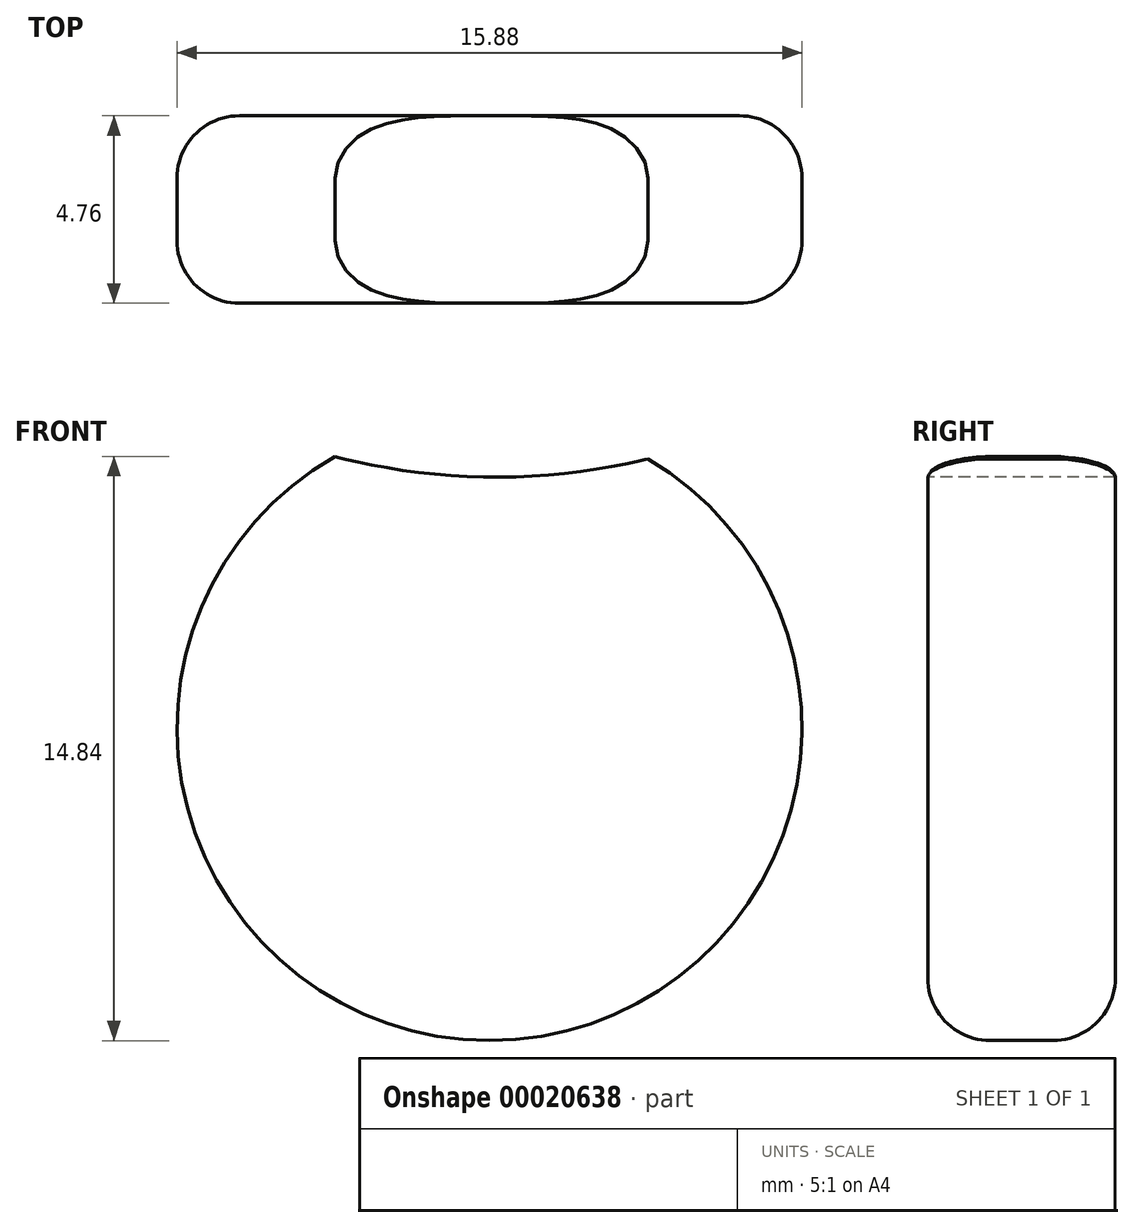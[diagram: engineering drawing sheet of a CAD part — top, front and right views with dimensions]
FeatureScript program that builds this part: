
annotation { "Feature Type Name" : "Feature", "Feature Type Description" : "" }
export const myFeature = defineFeature(function(context is Context, id is Id, definition is map)
    precondition{}
    {
        {
            var Q0;
            Q0=qCreatedBy(makeId("Front.planeOp"),FACE);
            var sketch = newSketch(context, id + "F0", { "sketchPlane" : qUnion([Q0])});
            skCircle(sketch, "E0", {"center": v(0, 0) * mm, "radius": 7.94 * mm});
            skSolve(sketch);
        }
        {
            var Q0;
            Q0=makeQuery(id+"F0.imprint","IMPRINT",FACE,{"disambiguationData":[TD([[makeQuery(id+"F0.imprint","IMPRINT",EDGE,{"derivedFrom":sQuery(id+"F0.wireOp",EDGE,"E0")}),1.0]])]});
            var sketch = newSketch(context, id + "F1", { "sketchPlane" : qUnion([Q0])});
            skSolve(sketch);
        }
        {
            var Q0;
            Q0 = qSketchRegion(id + "F1", true);
            var Q1;
            Q1=makeQuery(id+"F0.imprint","IMPRINT",FACE,{"disambiguationData":[TD([[makeQuery(id+"F0.imprint","IMPRINT",EDGE,{"derivedFrom":sQuery(id+"F0.wireOp",EDGE,"E0")}),1.0]])]});
            extrude(context, id + "F2", {"entities" : qUnion([Q0, Q1]), "depth" : 4.76 * mm});
        }
        {
            var Q0;
            Q0=makeQuery(id+"F2.opExtrude","CAP_EDGE",EDGE,{"disambiguationData":[OSD([sQuery(id+"F0.wireOp",EDGE,"E0")])],"isStart":false});
            fillet(context, id + "F3", {"entities" : qUnion([Q0]), "radius" : 1.59 * mm, "tangentPropagation" : true, "allowEdgeOverflow" : false});
        }
        {
            var Q0;
            Q0=makeQuery(id+"F2.opExtrude","CAP_EDGE",EDGE,{"disambiguationData":[OSD([sQuery(id+"F0.wireOp",EDGE,"E0")])],"isStart":true});
            fillet(context, id + "F4", {"entities" : qUnion([Q0]), "radius" : 1.59 * mm, "tangentPropagation" : true, "allowEdgeOverflow" : false});
        }
        {
            var Q0;
            Q0=makeQuery(id+"F2.opExtrude","CAP_FACE",FACE,{"disambiguationData":[OSD([sQuery(id+"F0.wireOp",EDGE,"E0")])],"isStart":false});
            var sketch = newSketch(context, id + "F5", { "sketchPlane" : qUnion([Q0])});
            skArc(sketch, "E1", {"start": v(-4.07, 6.94) * mm, "mid": v(0, 6.38) * mm, "end": v(4.07, 6.85) * mm});
            skArc(sketch, "E2", {"start": v(4.07, 6.85) * mm, "mid": v(0.02, 8.3) * mm, "end": v(-4.07, 6.94) * mm});
            skSolve(sketch);
        }
        {
            var Q0;
            Q0=makeQuery(id+"F5.imprint","IMPRINT",FACE,{"disambiguationData":[TD([[makeQuery(id+"F5.imprint","IMPRINT",EDGE,{"derivedFrom":sQuery(id+"F5.wireOp",EDGE,"69e19ec6-ee87-4225-b32f-7d6028c96ad0")}),1.0]])]});
            var Q1;
            Q1=makeQuery(id+"F5.imprint","IMPRINT",FACE,{"disambiguationData":[TD([[makeQuery(id+"F5.imprint","IMPRINT",EDGE,{"derivedFrom":sQuery(id+"F5.wireOp",EDGE,"E1")}),1.0]])]});
            extrude(context, id + "F6", {"entities" : qUnion([Q0, Q1]), "operationType" : NewBodyOperationType.REMOVE, "endBound" : BoundingType.THROUGH_ALL, "oppositeDirection" : true, "depth" : 25.4 * mm});
        }
    });
